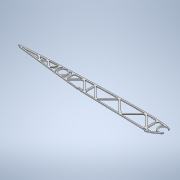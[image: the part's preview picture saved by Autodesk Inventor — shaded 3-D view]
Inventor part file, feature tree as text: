
AUTODESK INVENTOR PART (.ipt)
format: ipt  version: 2022 (Build 260153000, 153)  size: 473,088 bytes
history: native  units: mm
features: extrude x1, sketch x1
ambient origin geometry x8: Origin, YZ Plane, XZ Plane, XY Plane, X Axis, Y Axis, Z Axis, Center Point
bodies: Body1 (feature_tree)
feature tree (2):
  extrude  "Extrusion5"  Depth=10.0mm
  sketch  "Sketch1"  dims[d31=34.456mm d50=368.759386mm d57=16.0mm d69=8.0mm d80=19.0mm d81=16.0mm d82=1.0mm d83=1.0mm d84=1.0mm d85=1.0mm d86=1.0mm d87=0.8mm d88=1.0mm d90=19.0mm d94=5.0mm d95=5.0mm d105=5.0mm d106=5.0mm d108=2.0mm d114=5.0mm d115=5.0mm d116=24.0mm d117=2.5mm d118=2.5mm d123=2.5mm d124=2.5mm d125=10.0mm d126=24.0mm d127=24.0mm d128=27.0mm d135=0.5mm d139=7.0mm d169=27.0mm d181=45.0deg d185=7.0mm d186=45.0deg d190=7.0mm d191=45.0deg d206=90.0deg d212=90.0deg d215=7.0mm d216=90.0deg d219=7.0mm d220=2.0mm d221=0.0mm]
